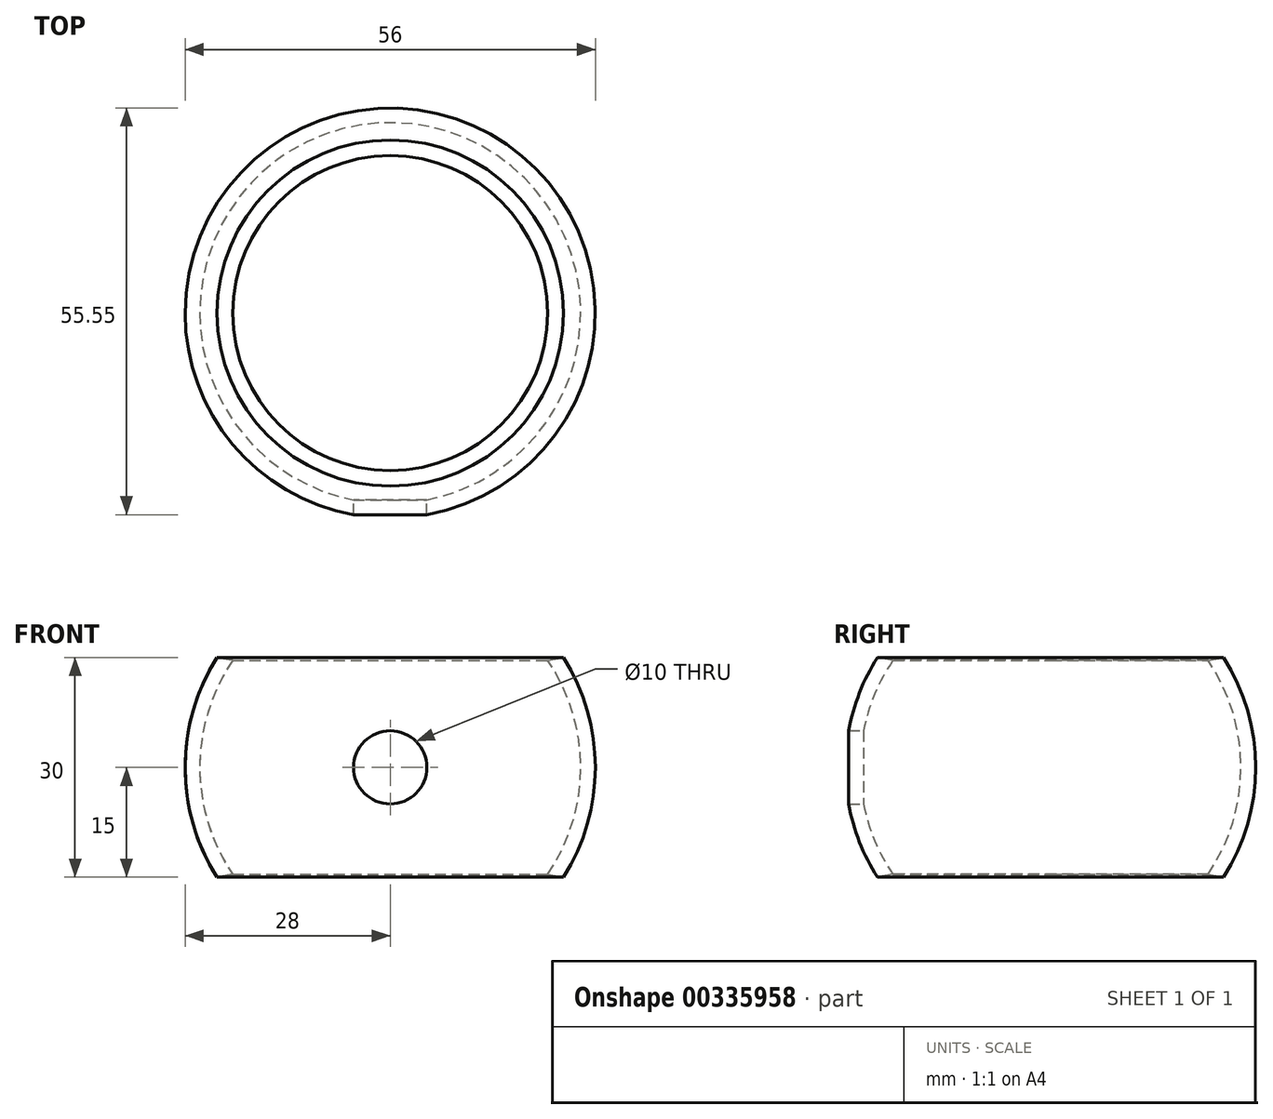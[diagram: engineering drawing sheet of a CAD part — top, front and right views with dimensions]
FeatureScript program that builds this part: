
annotation { "Feature Type Name" : "Feature", "Feature Type Description" : "" }
export const myFeature = defineFeature(function(context is Context, id is Id, definition is map)
    precondition{}
    {
        {
            var Q0;
            Q0=qCreatedBy(makeId("Front.planeOp"),FACE);
            var sketch = newSketch(context, id + "F0", { "sketchPlane" : qUnion([Q0])});
            skArc(sketch, "E0", {"start": v(23.64, 15) * mm, "mid": v(28, 0) * mm, "end": v(23.64, -15) * mm});
            skArc(sketch, "E1.0", {"start": v(21.5, 14.62) * mm, "mid": v(26, 0) * mm, "end": v(21.5, -14.62) * mm});
            skLineSegment(sketch, "E2", {"start": v(21.5, 14.62) * mm, "end": v(23.64, 15) * mm});
            skLineSegment(sketch, "E3", {"start": v(21.5, -14.62) * mm, "end": v(23.64, -15) * mm});
            skLineSegment(sketch, "E4", {"start": v(0, -17.87) * mm, "end": v(0, 15.39) * mm});
            skSolve(sketch);
        }
        {
            var Q0;
            Q0 = qSketchRegion(id + "F0", true);
            var Q1;
            Q1=sQuery(id+"F0.wireOp",EDGE,"E4");
            revolve(context, id + "F1", {"entities" : qUnion([Q0]), "axis" : qUnion([Q1]), "revolveType" : RevolveType.FULL});
        }
        {
            var Q0;
            Q0=qCreatedBy(makeId("Front.planeOp"),FACE);
            var sketch = newSketch(context, id + "F2", { "sketchPlane" : qUnion([Q0])});
            skCircle(sketch, "E5", {"center": v(0, 0) * mm, "radius": 5 * mm});
            skSolve(sketch);
        }
        {
            var Q0;
            Q0 = qSketchRegion(id + "F2", true);
            extrude(context, id + "F3", {"entities" : qUnion([Q0]), "operationType" : NewBodyOperationType.REMOVE, "depth" : 35.2 * mm});
        }
    });
